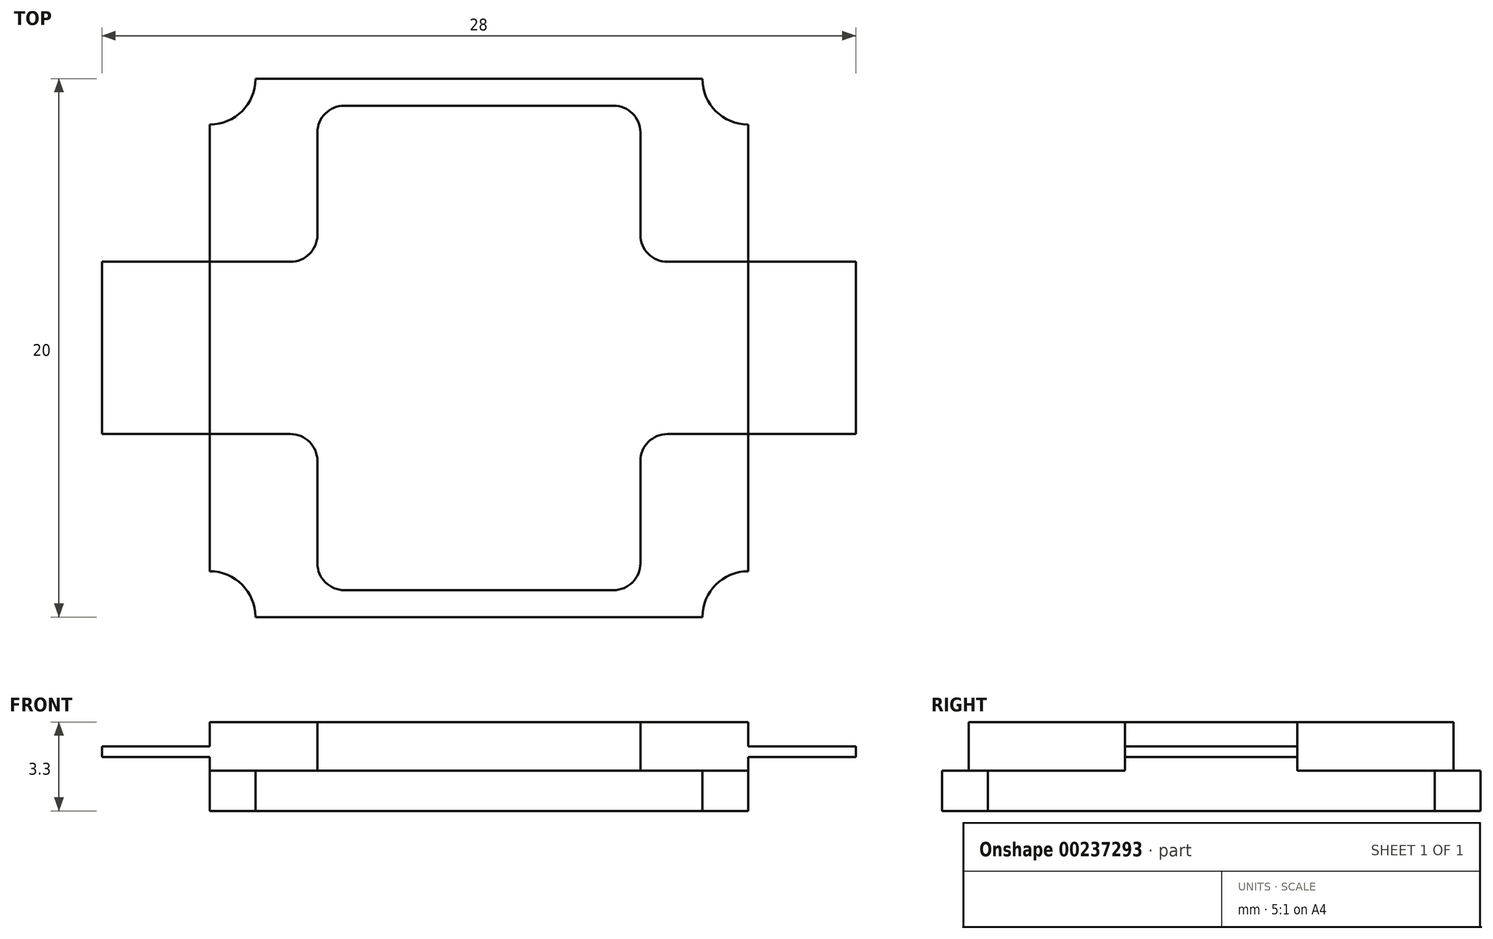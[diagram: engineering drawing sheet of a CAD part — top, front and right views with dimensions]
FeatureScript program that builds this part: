
annotation { "Feature Type Name" : "Feature", "Feature Type Description" : "" }
export const myFeature = defineFeature(function(context is Context, id is Id, definition is map)
    precondition{}
    {
        {
            var Q0;
            Q0=qCreatedBy(makeId("Top.planeOp"),FACE);
            var sketch = newSketch(context, id + "F0", { "sketchPlane" : qUnion([Q0])});
            skLineSegment(sketch, "E0.bottom", {"start": v(8.3, -10) * mm, "end": v(-8.3, -10) * mm});
            skLineSegment(sketch, "E0.top", {"start": v(8.3, 10) * mm, "end": v(-8.3, 10) * mm});
            skLineSegment(sketch, "E0.left", {"start": v(10, -8.3) * mm, "end": v(10, 8.3) * mm});
            skLineSegment(sketch, "E0.right", {"start": v(-10, -8.3) * mm, "end": v(-10, 8.3) * mm});
            skPoint(sketch, "E0.middle", {"position": v(0, 0) * mm});
            skArc(sketch, "E1", {"start": v(10, 8.3) * mm, "mid": v(8.8, 8.8) * mm, "end": v(8.3, 10) * mm});
            skArc(sketch, "E2.1.0", {"start": v(-8.3, 10) * mm, "mid": v(-8.8, 8.8) * mm, "end": v(-10, 8.3) * mm});
            skArc(sketch, "E2.2.0", {"start": v(-10, -8.3) * mm, "mid": v(-8.8, -8.8) * mm, "end": v(-8.3, -10) * mm});
            skArc(sketch, "E2.3.0", {"start": v(8.3, -10) * mm, "mid": v(8.8, -8.8) * mm, "end": v(10, -8.3) * mm});
            skSolve(sketch);
        }
        {
            var Q0;
            Q0=makeQuery(id+"F0.imprint","IMPRINT",FACE,{"disambiguationData":[TD([[makeQuery(id+"F0.imprint","IMPRINT",EDGE,{"derivedFrom":sQuery(id+"F0.wireOp",EDGE,"E0.bottom")}),-1.0]])]});
            extrude(context, id + "F1", {"entities" : qUnion([Q0]), "oppositeDirection" : true, "depth" : 1.5 * mm});
        }
        {
            var Q0;
            Q0=makeQuery(id+"F1.opExtrude","CAP_FACE",FACE,{"disambiguationData":[OSD([sQuery(id+"F0.wireOp",EDGE,"E0.bottom"),sQuery(id+"F0.wireOp",EDGE,"E0.top"),sQuery(id+"F0.wireOp",EDGE,"E0.left"),sQuery(id+"F0.wireOp",EDGE,"E0.right"),sQuery(id+"F0.wireOp",EDGE,"E1"),sQuery(id+"F0.wireOp",EDGE,"E2.1.0"),sQuery(id+"F0.wireOp",EDGE,"E2.2.0"),sQuery(id+"F0.wireOp",EDGE,"E2.3.0")])],"isStart":true});
            var sketch = newSketch(context, id + "F2", { "sketchPlane" : qUnion([Q0])});
            skLineSegment(sketch, "E3.bottom", {"start": v(5, -9) * mm, "end": v(-5, -9) * mm});
            skLineSegment(sketch, "E3.top", {"start": v(5, 9) * mm, "end": v(-5, 9) * mm});
            skLineSegment(sketch, "E3.left", {"start": v(6, -8) * mm, "end": v(6, -4.2) * mm});
            skLineSegment(sketch, "E3.right", {"start": v(-6, -8) * mm, "end": v(-6, -4.2) * mm});
            skPoint(sketch, "E3.middle", {"position": v(0, 0) * mm});
            skLineSegment(sketch, "E4.bottom", {"start": v(10, -3.2) * mm, "end": v(7, -3.2) * mm});
            skLineSegment(sketch, "E4.top", {"start": v(10, 3.2) * mm, "end": v(7, 3.2) * mm});
            skLineSegment(sketch, "E4.left", {"start": v(10, -3.2) * mm, "end": v(10, 3.2) * mm});
            skLineSegment(sketch, "E4.right", {"start": v(-10, -3.2) * mm, "end": v(-10, 3.2) * mm});
            skLineSegment(sketch, "E5.trimOffspring", {"start": v(6, 4.2) * mm, "end": v(6, 8) * mm});
            skLineSegment(sketch, "E6.trimOffspring", {"start": v(-7, 3.2) * mm, "end": v(-10, 3.2) * mm});
            skLineSegment(sketch, "E7.trimOffspring", {"start": v(-6, 4.2) * mm, "end": v(-6, 8) * mm});
            skLineSegment(sketch, "E8.trimOffspring", {"start": v(-7, -3.2) * mm, "end": v(-10, -3.2) * mm});
            skPoint(sketch, "E9.visualSharp", {"position": v(-6, -9) * mm});
            skArc(sketch, "E9.filletArc", {"start": v(-6, -8) * mm, "mid": v(-5.7, -8.7) * mm, "end": v(-5, -9) * mm});
            skPoint(sketch, "E10.visualSharp", {"position": v(6, -9) * mm});
            skArc(sketch, "E10.filletArc", {"start": v(5, -9) * mm, "mid": v(5.7, -8.7) * mm, "end": v(6, -8) * mm});
            skPoint(sketch, "E11.visualSharp", {"position": v(6, 3.2) * mm});
            skArc(sketch, "E11.filletArc", {"start": v(6, 4.2) * mm, "mid": v(6.3, 3.5) * mm, "end": v(7, 3.2) * mm});
            skPoint(sketch, "E12.visualSharp", {"position": v(6, 9) * mm});
            skArc(sketch, "E12.filletArc", {"start": v(6, 8) * mm, "mid": v(5.7, 8.7) * mm, "end": v(5, 9) * mm});
            skPoint(sketch, "E13.visualSharp", {"position": v(-6, 9) * mm});
            skArc(sketch, "E13.filletArc", {"start": v(-5, 9) * mm, "mid": v(-5.7, 8.7) * mm, "end": v(-6, 8) * mm});
            skPoint(sketch, "E14.visualSharp", {"position": v(-6, 3.2) * mm});
            skArc(sketch, "E14.filletArc", {"start": v(-7, 3.2) * mm, "mid": v(-6.3, 3.5) * mm, "end": v(-6, 4.2) * mm});
            skPoint(sketch, "E15.visualSharp", {"position": v(-6, -3.2) * mm});
            skArc(sketch, "E15.filletArc", {"start": v(-6, -4.2) * mm, "mid": v(-6.3, -3.5) * mm, "end": v(-7, -3.2) * mm});
            skPoint(sketch, "E16.visualSharp", {"position": v(6, -3.2) * mm});
            skArc(sketch, "E16.filletArc", {"start": v(7, -3.2) * mm, "mid": v(6.3, -3.5) * mm, "end": v(6, -4.2) * mm});
            skSolve(sketch);
        }
        {
            var Q0;
            Q0=makeQuery(id+"F2.imprint","IMPRINT",FACE,{"disambiguationData":[TD([[makeQuery(id+"F2.imprint","IMPRINT",EDGE,{"derivedFrom":sQuery(id+"F2.wireOp",EDGE,"E3.bottom")}),-1.0]])]});
            extrude(context, id + "F3", {"entities" : qUnion([Q0]), "operationType" : NewBodyOperationType.ADD, "depth" : 1.8 * mm});
        }
        {
            var Q0;
            Q0=makeQuery(id+"F3.boolean.opBoolean","MERGE",FACE,{"derivedFrom":[makeQuery(id+"F1.opExtrude","SWEPT_FACE",FACE,{"disambiguationData":[OSD([sQuery(id+"F0.wireOp",EDGE,"E0.right")])]}),makeQuery(id+"F3.opExtrude","SWEPT_FACE",FACE,{"disambiguationData":[OSD([sQuery(id+"F2.wireOp",EDGE,"E4.right")])]})]});
            var sketch = newSketch(context, id + "F4", { "sketchPlane" : qUnion([Q0])});
            skLineSegment(sketch, "E17.bottom", {"start": v(3.2, 0.5) * mm, "end": v(-3.2, 0.5) * mm});
            skLineSegment(sketch, "E17.top", {"start": v(3.2, 0.9) * mm, "end": v(-3.2, 0.9) * mm});
            skLineSegment(sketch, "E17.left", {"start": v(3.2, 0.5) * mm, "end": v(3.2, 0.9) * mm});
            skLineSegment(sketch, "E17.right", {"start": v(-3.2, 0.5) * mm, "end": v(-3.2, 0.9) * mm});
            skPoint(sketch, "E17.middle", {"position": v(0, 0.7) * mm});
            skSolve(sketch);
        }
        {
            var Q0;
            Q0=makeQuery(id+"F4.imprint","IMPRINT",FACE,{"disambiguationData":[TD([[makeQuery(id+"F4.imprint","IMPRINT",EDGE,{"derivedFrom":sQuery(id+"F4.wireOp",EDGE,"E17.bottom")}),-1.0]])]});
            extrude(context, id + "F5", {"entities" : qUnion([Q0]), "operationType" : NewBodyOperationType.ADD, "depth" : 4 * mm});
        }
        {
            var Q0;
            Q0 = qSketchRegion(id + "F4", true);
            extrude(context, id + "F6", {"entities" : qUnion([Q0]), "operationType" : NewBodyOperationType.ADD, "oppositeDirection" : true, "depth" : 24 * mm});
        }
    });
